# Revit family: METALFIRE_AVENUE_MF_GHE_2S
name_source: partatom
category: Mechanical Equipment
revit_build: Autodesk Revit 2017 (Build: 20160225_1515(x64)
units: mm (PartAtom-declared; Revit-internal decimal feet)

## family parameters
Always vertical = Yes
Cut with Voids When Loaded = No
Host = Wall
OmniClass Number = 23.75.00.00
OmniClass Title = Climate Control (HVAC)
Part Type = Normal
Room Calculation Point = Yes
Round Connector Dimension = Use Diameter
Shared = No

## types (8) — shared parameters
BIM BADGE = https://bim.archiproducts.com
Description = The Avenue represents the gas-fired high efficiency closed fireplaces in the Metalfire range.
FINISHING MATERIAL = Black painted vermiculite plates - Metalfire
FRAME MATERIAL = Iron - Metalfire
MATERIAL DESCRIPTION = Iron, galvanized steel and vermiculite plates
Manufacturer = Metalfire
Model = Avenue
OVERALL DEPTH = 444 mm
PRODUCT SHEET = https://www.archiproducts.com
SMOKE EXHAUST = Ø130/200 mm
TECHNICAL SHEET = https://www.metalfire.eu
URL = https://www.metalfire.eu

## per-type parameters (varying)
| type | DEPTH | EFFICIENCY | ENERGY EFFICIENCY CLASS | HEIGHT | OUTPUT | OVERALL HEIGHT | OVERALL WIDTH | PRODUCT CODE | WEIGHT | WIDTH |
| 1050 x 750 mm | 336 mm | 87.00% | A (G20) / B (G30) | 740 mm | 9.5 kW | 1120 mm | 1178 mm | MF 1050-75 GHE 2S | 150.00 kg | 1094 mm |
| 800 x 750 mm | 336 mm | 84.50% | B | 740 mm | 8.1 kW | 1120 mm | 928 mm | MF 800-75 GHE 2S | 100.00 kg | 844 mm |
| 900 x 600 mm | 330 mm | 84.50% | B | 590 mm | 8.1 kW | 970 mm | 1028 mm | MF 900-60 GHE 2S | 100.00 kg | 950 mm |
| 1050 x 400 mm | 336 mm | 84.80% | B | 390 mm | 8.0 kW | 770 mm | 1178 mm | MF 1050-40 GHE 2S | 100.00 kg | 1094 mm |
| 1050 x 600 mm | 336 mm | 87.00% | A (G20) / B (G30) | 590 mm | 9.5 kW | 970 mm | 1178 mm | MF 1050-60 GHE 2S | 150.00 kg | 1094 mm |
| 1300 x 400 mm | 336 mm | 82.00% | B | 390 mm | 8.4 kW | 770 mm | 1428 mm | MF 1300-40 GHE 2S | 100.00 kg | 1344 mm |
| 1300 x 600 mm | 336 mm | 87.00% | A (G20) / B (G30) | 590 mm | 9.5 kW | 970 mm | 1428 mm | MF 1300-60 GHE 2S | 150.00 kg | 1344 mm |
| 1600 x 400 mm | 336 mm | 83.30% | B | 390 mm | 9.5 kW | 770 mm | 1728 mm | MF 1600-40 GHE 2S | 150.00 kg | 1644 mm |

## geometry (parser evidence)
native form markers: Sweep x4
no freeform markers — native parametric forms only
